# Revit family: Shower-Valve_Trim-KOHLER-Singulier-K-T10449
name_source: partatom
category: Specialty Equipment
revit_build: Autodesk Revit 2017 (Build: 20160225_1515(x64)
units: mm (PartAtom-declared; Revit-internal decimal feet)

## family parameters
Cut with Voids When Loaded = No
Host = Face
OmniClass Number = 23.31.25.00
OmniClass Title = Toilet and Bath Specialties
Part Type = Normal
Room Calculation Point = No
Round Connector Dimension = Use Diameter
Shared = No

## types (1)
- CP-Polished Chrome
    ADA Compliant = Yes
    Assembly Code = C1030200
    Date Modified = 02/08/2021
    Default Elevation = 42"
    Description = Transfer valve trim
    Finish = Kohler-Metal-CP-Polished_Chrome
    Handle Clerance = 3 1/2"
    Height = 5 1/2"
    Length = 3 3/8"
    Manufacturer = KOHLER Co.
    Master Format 2014 = 10 28 00
    Master Format 2014 Name = Toilet, Bath, and Laundry Accessories
    Material = Premium Metal Construction
    Model = K-T10449-4-CP
    Product Documentation Link = https://www.us.kohler.com
    Product Name = Singulier
    Product Page URL = http://www.us.kohler.com
    Type = 1
    URL = https://www.us.kohler.com
    WaterSense Certified = No
    Width = 5"

## geometry (parser evidence)
native form markers: Sweep x5
no freeform markers — native parametric forms only
